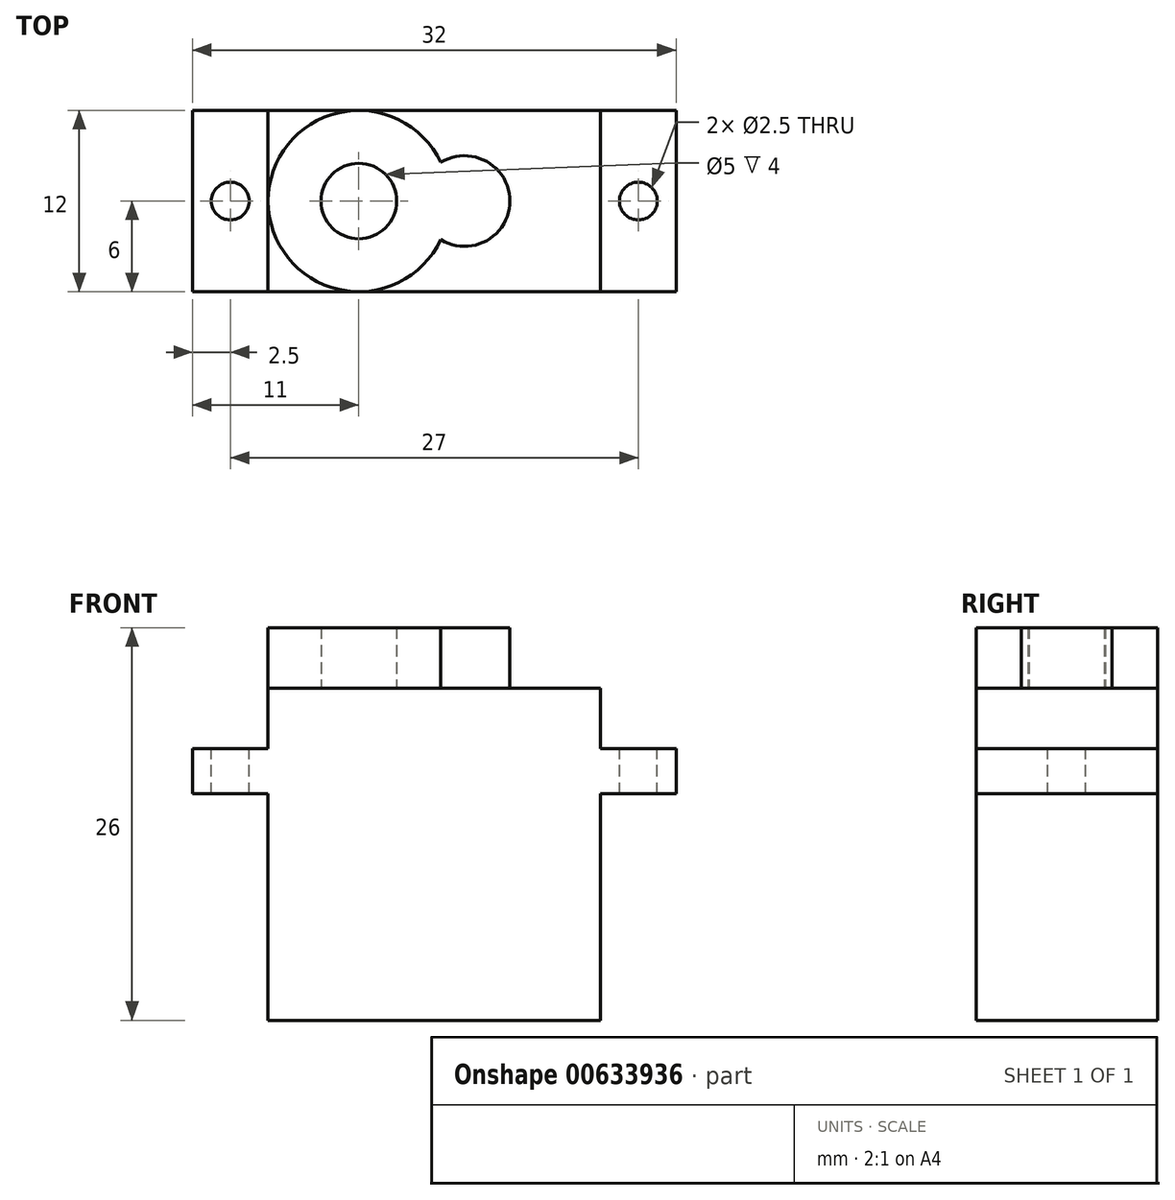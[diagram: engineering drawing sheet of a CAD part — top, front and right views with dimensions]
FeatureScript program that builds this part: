
annotation { "Feature Type Name" : "Feature", "Feature Type Description" : "" }
export const myFeature = defineFeature(function(context is Context, id is Id, definition is map)
    precondition{}
    {
        {
            var Q0;
            Q0=qCreatedBy(makeId("Top.planeOp"),FACE);
            var sketch = newSketch(context, id + "F0", { "sketchPlane" : qUnion([Q0])});
            skLineSegment(sketch, "E0.bottom", {"start": v(-11, -6) * mm, "end": v(11, -6) * mm});
            skLineSegment(sketch, "E0.top", {"start": v(-11, 6) * mm, "end": v(11, 6) * mm});
            skLineSegment(sketch, "E0.left", {"start": v(-11, -6) * mm, "end": v(-11, 6) * mm});
            skLineSegment(sketch, "E0.right", {"start": v(11, -6) * mm, "end": v(11, 6) * mm});
            skSolve(sketch);
        }
        {
            var Q0;
            Q0 = qSketchRegion(id + "F0", true);
            extrude(context, id + "F1", {"entities" : qUnion([Q0]), "depth" : 22 * mm, "offsetDistance" : 25 * mm});
        }
        {
            var Q0;
            Q0=makeQuery(id+"F1.opExtrude","CAP_FACE",FACE,{"disambiguationData":[OSD([sQuery(id+"F0.wireOp",EDGE,"E0.bottom"),sQuery(id+"F0.wireOp",EDGE,"E0.top"),sQuery(id+"F0.wireOp",EDGE,"E0.left"),sQuery(id+"F0.wireOp",EDGE,"E0.right")])],"isStart":false});
            var sketch = newSketch(context, id + "F2", { "sketchPlane" : qUnion([Q0])});
            skLineSegment(sketch, "E1", {"start": v(-11, 0) * mm, "end": v(-5, 0) * mm, "construction": true});
            skArc(sketch, "E2", {"start": v(0.43, 2.56) * mm, "mid": v(-11, 0) * mm, "end": v(0.43, -2.56) * mm});
            skLineSegment(sketch, "E3", {"start": v(-5, 0) * mm, "end": v(2, 0) * mm, "construction": true});
            skArc(sketch, "E4", {"start": v(0.43, -2.56) * mm, "mid": v(5, 0) * mm, "end": v(0.43, 2.56) * mm});
            skCircle(sketch, "E5", {"center": v(-5, 0) * mm, "radius": 2.5 * mm});
            skSolve(sketch);
        }
        {
            var Q0;
            Q0 = qSketchRegion(id + "F2", true);
            extrude(context, id + "F3", {"entities" : qUnion([Q0]), "operationType" : NewBodyOperationType.ADD, "depth" : 4 * mm, "offsetDistance" : 25 * mm});
        }
        {
            var Q0;
            Q0=makeQuery(id+"F1.opExtrude","SWEPT_FACE",FACE,{"disambiguationData":[OSD([sQuery(id+"F0.wireOp",EDGE,"E0.left")])]});
            var sketch = newSketch(context, id + "F4", { "sketchPlane" : qUnion([Q0])});
            skLineSegment(sketch, "E6", {"start": v(-6, 0) * mm, "end": v(-6, 15) * mm, "construction": true});
            skLineSegment(sketch, "E7", {"start": v(-6, 15) * mm, "end": v(6, 15) * mm});
            skLineSegment(sketch, "E8", {"start": v(6, 15) * mm, "end": v(6, 18) * mm});
            skLineSegment(sketch, "E9", {"start": v(6, 18) * mm, "end": v(-6, 18) * mm});
            skLineSegment(sketch, "E10", {"start": v(-6, 18) * mm, "end": v(-6, 15) * mm});
            skSolve(sketch);
        }
        {
            var Q0;
            Q0 = qSketchRegion(id + "F4", true);
            extrude(context, id + "F5", {"entities" : qUnion([Q0]), "operationType" : NewBodyOperationType.ADD, "depth" : 5 * mm, "offsetDistance" : 25 * mm, "hasSecondDirection" : true, "secondDirectionOppositeDirection" : true, "secondDirectionDepth" : 27 * mm});
        }
        {
            var Q0;
            {var subQ1=sQuery(id+"F4.wireOp",EDGE,"E9");Q0=makeQuery(id+"F5.boolean.opBoolean","SPLIT",FACE,{"disambiguationData":[TD([makeQuery(id+"F1.opExtrude","SWEPT_FACE",FACE,{"disambiguationData":[OSD([sQuery(id+"F0.wireOp",EDGE,"E0.right")])]})])],"derivedFrom":makeQuery(id+"F5.opExtrude","SWEPT_FACE",FACE,{"disambiguationData":[OSD([subQ1])]})});}
            var sketch = newSketch(context, id + "F6", { "sketchPlane" : qUnion([Q0])});
            skLineSegment(sketch, "E11", {"start": v(16, 0) * mm, "end": v(11, 0) * mm, "construction": true});
            skLineSegment(sketch, "E12", {"start": v(13.5, 0) * mm, "end": v(13.5, 2.7) * mm, "construction": true});
            skLineSegment(sketch, "E13", {"start": v(13.5, 0) * mm, "end": v(13.5, -3.04) * mm, "construction": true});
            skSolve(sketch);
        }
        {
            var Q0;
            {var subQ1=sQuery(id+"F4.wireOp",EDGE,"E9");Q0=makeQuery(id+"F5.boolean.opBoolean","SPLIT",FACE,{"disambiguationData":[TD([makeQuery(id+"F1.opExtrude","SWEPT_FACE",FACE,{"disambiguationData":[OSD([sQuery(id+"F0.wireOp",EDGE,"E0.left")])]})])],"derivedFrom":makeQuery(id+"F5.opExtrude","SWEPT_FACE",FACE,{"disambiguationData":[OSD([subQ1])]})});}
            var sketch = newSketch(context, id + "F7", { "sketchPlane" : qUnion([Q0])});
            skLineSegment(sketch, "E14", {"start": v(-16, 0) * mm, "end": v(-11, 0) * mm, "construction": true});
            skLineSegment(sketch, "E15", {"start": v(-11, 0) * mm, "end": v(-13.5, 0) * mm});
            skLineSegment(sketch, "E16", {"start": v(-13.5, 0) * mm, "end": v(-13.5, -2.58) * mm, "construction": true});
            skLineSegment(sketch, "E17", {"start": v(-13.5, 0) * mm, "end": v(-13.5, 3.08) * mm, "construction": true});
            skSolve(sketch);
        }
        {
            var Q0;
            Q0=sQuery(id+"F6.wireOp",VERTEX,"E13.start");
            var Q1;
            Q1=sQuery(id+"F7.wireOp",VERTEX,"E17.start");
            var Q2;
            Q2=makeQuery(id+"F1.opExtrude","SWEPT_BODY",BODY,{"disambiguationData":[OSD([sQuery(id+"F0.wireOp",EDGE,"E0.bottom"),sQuery(id+"F0.wireOp",EDGE,"E0.top"),sQuery(id+"F0.wireOp",EDGE,"E0.left"),sQuery(id+"F0.wireOp",EDGE,"E0.right")])]});
            hole(context, id + "F8", {"style" : HoleStyle.SIMPLE, "endStyle" : HoleEndStyle.THROUGH, "holeDiameter" : 2.5 * mm, "majorDiameter" : 5 * mm, "isTappedThrough" : true, "tappedDepth" : 12 * mm, "tapClearance" : 3, "locations" : qUnion([Q0, Q1]), "scope" : qUnion([Q2])});
        }
    });
